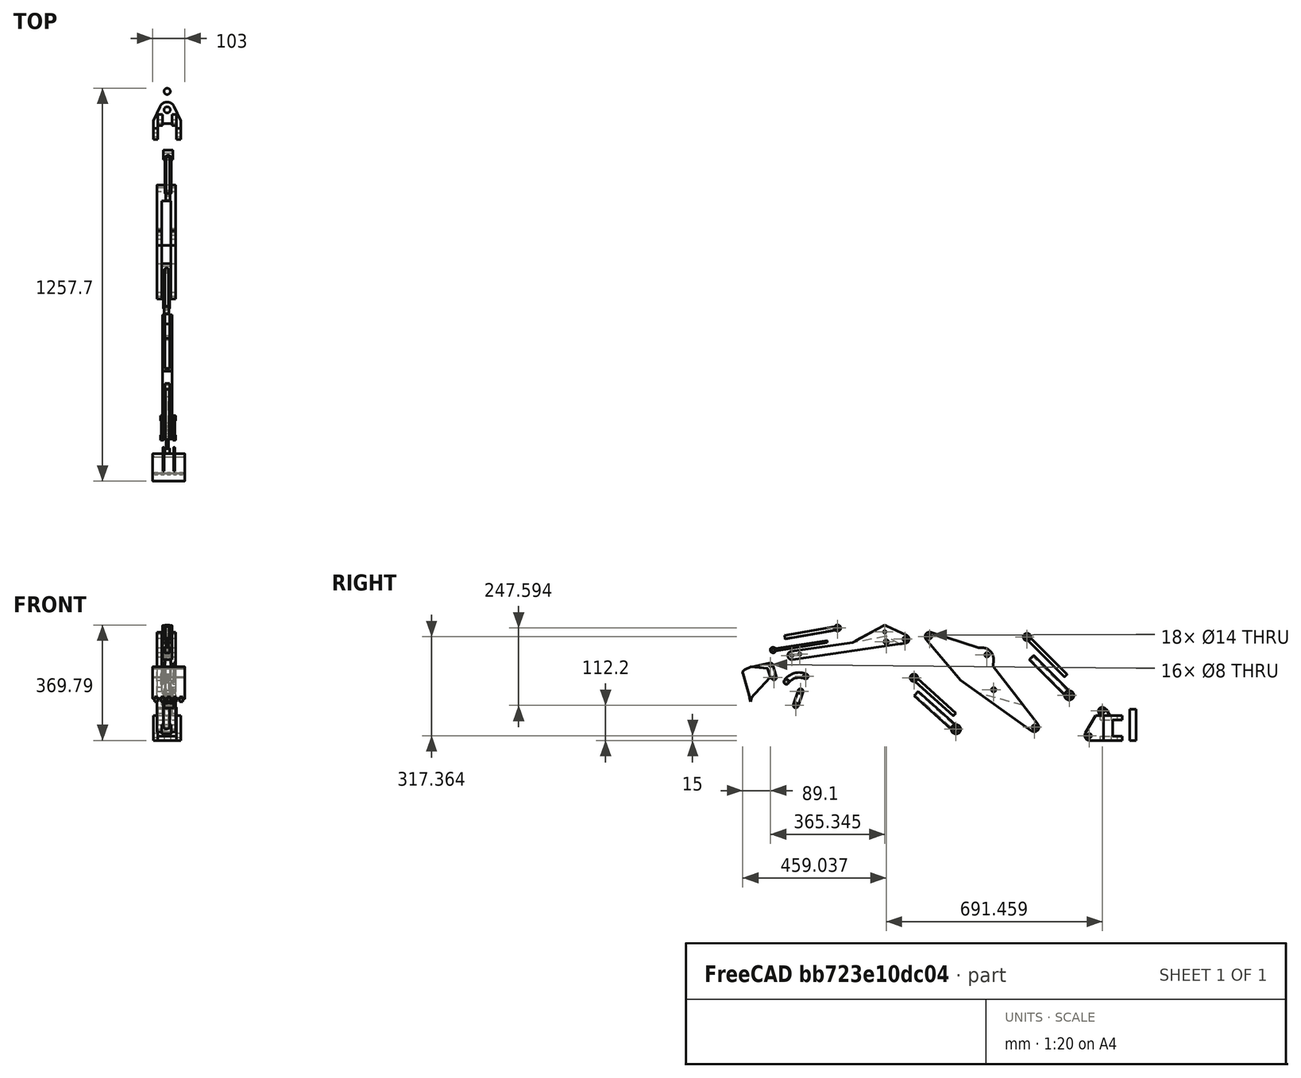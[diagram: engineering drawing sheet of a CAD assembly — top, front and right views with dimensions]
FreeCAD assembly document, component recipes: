
FREECAD ASSEMBLY — COMPONENT RECIPES ("AssemblyExample")

This assembly document has 13 components, labeled P0..P12 below (a component is one placed body or linked part). 0 of them carry a construction recipe — the FreeCAD feature program that regenerates the part from scratch, quoted from this document or its linked companion documents; the rest are supplied as boundary geometry only. No exploded tour is included for this assembly.
COMPONENT P0 — geometry summary ("Base001"; no construction recipe available for this part):
  bounding box: 119.7 x 106.0 x 88.3 mm
  tessellated surface: 4,364 triangles
  volume: 241281 mm^3 (22% of its bounding box)
  symmetry: mirror-symmetric across its x mid-plane
COMPONENT P1 — geometry summary ("BasePin001"; no construction recipe available for this part):
  bounding box: 100.0 x 20.0 x 20.0 mm
  tessellated surface: 500 triangles
  volume: 31416 mm^3 (79% of its bounding box)
  symmetry: 2-fold rotationally symmetric about the x axis; revolution-symmetric about the z axis through its bounding-box center; mirror-symmetric across its x mid-plane, y mid-plane, z mid-plane
COMPONENT P2 — geometry summary ("Boom001"; no construction recipe available for this part):
  bounding box: 436.3 x 203.7 x 60.9 mm
  tessellated surface: 4,520 triangles
  volume: 1204575 mm^3 (22% of its bounding box)
  symmetry: mirror-symmetric across its x mid-plane
COMPONENT P3 — geometry summary ("BoomCylinderInner001"; no construction recipe available for this part):
  bounding box: 177.3 x 82.0 x 15.1 mm
  tessellated surface: 1,472 triangles
  volume: 22989 mm^3 (10% of its bounding box)
COMPONENT P4 — geometry summary ("BoomCylinderOuter001"; no construction recipe available for this part):
  bounding box: 177.7 x 87.1 x 30.1 mm
  tessellated surface: 1,966 triangles
  volume: 48197 mm^3 (10% of its bounding box)
  symmetry: mirror-symmetric across its x mid-plane
COMPONENT P5 — geometry summary ("Bucket001"; no construction recipe available for this part):
  bounding box: 117.6 x 103.4 x 100.6 mm
  tessellated surface: 3,994 triangles
  volume: 58312 mm^3 (5% of its bounding box)
  symmetry: mirror-symmetric across its x mid-plane
COMPONENT P6 — geometry summary ("BucketCylinderInner001"; no construction recipe available for this part):
  bounding box: 173.2 x 77.1 x 15.1 mm
  tessellated surface: 1,172 triangles
  volume: 9046 mm^3 (4% of its bounding box)
COMPONENT P7 — geometry summary ("BucketCylinderOuter001"; no construction recipe available for this part):
  bounding box: 171.1 x 78.8 x 15.1 mm
  tessellated surface: 1,556 triangles
  volume: 16012 mm^3 (8% of its bounding box)
COMPONENT P8 — geometry summary ("BucketLink004"; no construction recipe available for this part):
  bounding box: 62.9 x 30.3 x 26.8 mm
  tessellated surface: 3,660 triangles
  volume: 12304 mm^3 (24% of its bounding box)
  symmetry: mirror-symmetric across its x mid-plane
COMPONENT P9 — geometry summary ("BucketLink003"; no construction recipe available for this part):
  bounding box: 73.0 x 48.2 x 47.1 mm
  tessellated surface: 4,321 triangles
  volume: 17079 mm^3 (10% of its bounding box)
COMPONENT P10 — geometry summary ("Stick001"; no construction recipe available for this part):
  bounding box: 379.8 x 121.2 x 31.8 mm
  tessellated surface: 3,756 triangles
  volume: 333942 mm^3 (23% of its bounding box)
COMPONENT P11 — geometry summary ("StickCylinderInner001"; no construction recipe available for this part):
  bounding box: 184.3 x 56.4 x 15.1 mm
  tessellated surface: 1,472 triangles
  volume: 22989 mm^3 (15% of its bounding box)
COMPONENT P12 — geometry summary ("StickCylinderOuter001"; no construction recipe available for this part):
  bounding box: 184.0 x 62.4 x 30.1 mm
  tessellated surface: 1,966 triangles
  volume: 48197 mm^3 (14% of its bounding box)
  symmetry: mirror-symmetric across its x mid-plane
PROVENANCE & LICENSES
A FreeCAD (.FCStd) document from a public repository crawl; recipes are the document's own serialized feature recipes (and, for linked parts, companion documents' recipes).
License: gpl-2.0.
